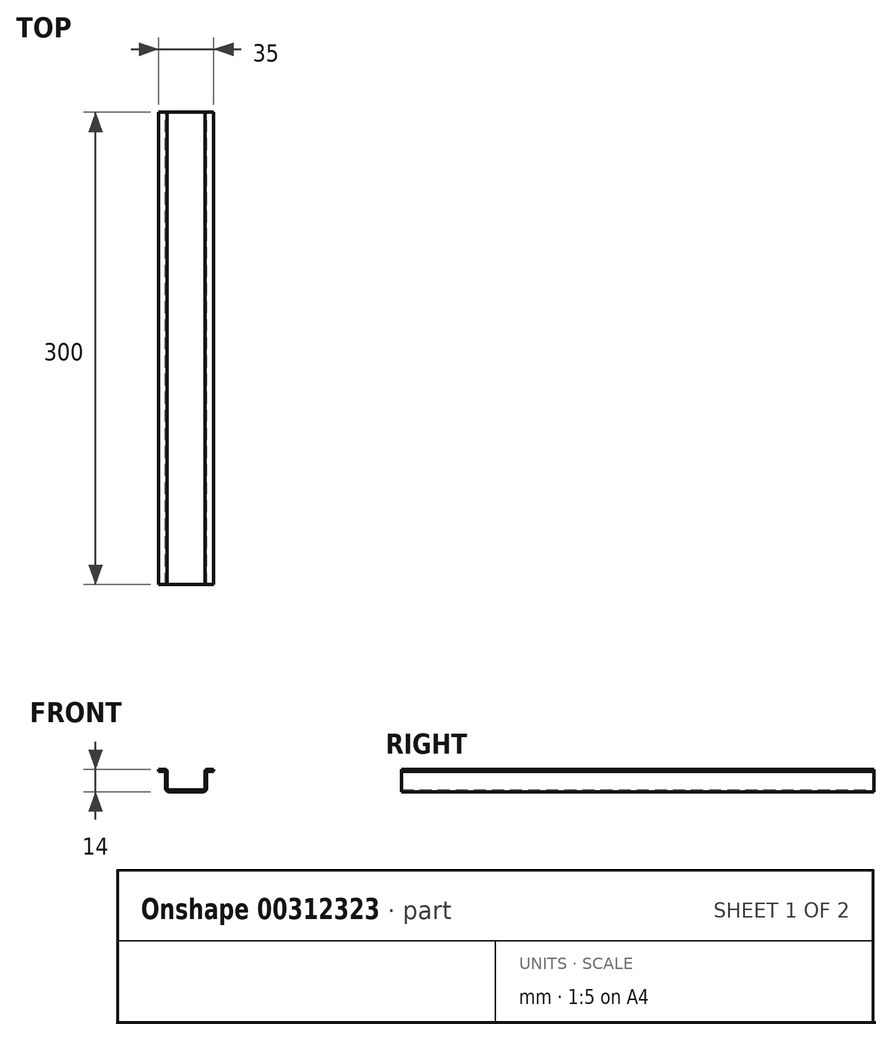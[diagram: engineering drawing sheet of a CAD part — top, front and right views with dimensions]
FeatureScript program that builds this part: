
annotation { "Feature Type Name" : "Feature", "Feature Type Description" : "" }
export const myFeature = defineFeature(function(context is Context, id is Id, definition is map)
    precondition{}
    {
        {
            var Q0;
            Q0=qCreatedBy(makeId("Front.planeOp"),FACE);
            var sketch = newSketch(context, id + "F0", { "sketchPlane" : qUnion([Q0])});
            skLineSegment(sketch, "E0", {"start": v(0, 0) * mm, "end": v(4.5, 0) * mm});
            skLineSegment(sketch, "E1", {"start": v(5.5, -1) * mm, "end": v(5.5, -12) * mm});
            skLineSegment(sketch, "E2", {"start": v(6.5, -13) * mm, "end": v(28.5, -13) * mm});
            skLineSegment(sketch, "E3", {"start": v(29.5, -12) * mm, "end": v(29.5, -1) * mm});
            skLineSegment(sketch, "E4", {"start": v(30.5, 0) * mm, "end": v(35, 0) * mm});
            skPoint(sketch, "E5.visualSharp", {"position": v(5.5, 0) * mm});
            skArc(sketch, "E5.filletArc", {"start": v(5.5, -1) * mm, "mid": v(5.2, -0.3) * mm, "end": v(4.5, 0) * mm});
            skPoint(sketch, "E6.visualSharp", {"position": v(5.5, -13) * mm});
            skArc(sketch, "E6.filletArc", {"start": v(5.5, -12) * mm, "mid": v(5.8, -12.7) * mm, "end": v(6.5, -13) * mm});
            skPoint(sketch, "E7.visualSharp", {"position": v(29.5, -13) * mm});
            skArc(sketch, "E7.filletArc", {"start": v(28.5, -13) * mm, "mid": v(29.2, -12.7) * mm, "end": v(29.5, -12) * mm});
            skPoint(sketch, "E8.visualSharp", {"position": v(29.5, 0) * mm});
            skArc(sketch, "E8.filletArc", {"start": v(30.5, 0) * mm, "mid": v(29.8, -0.3) * mm, "end": v(29.5, -1) * mm});
            skLineSegment(sketch, "E9.0", {"start": v(0, -1) * mm, "end": v(4.5, -1) * mm});
            skLineSegment(sketch, "E10.0", {"start": v(4.5, -1) * mm, "end": v(4.5, -12) * mm});
            skArc(sketch, "E11.0", {"start": v(4.5, -12) * mm, "mid": v(5.09, -13.41) * mm, "end": v(6.5, -14) * mm});
            skLineSegment(sketch, "E12.0", {"start": v(6.5, -14) * mm, "end": v(28.5, -14) * mm});
            skArc(sketch, "E13.0", {"start": v(28.5, -14) * mm, "mid": v(29.91, -13.41) * mm, "end": v(30.5, -12) * mm});
            skLineSegment(sketch, "E14.0", {"start": v(30.5, -12) * mm, "end": v(30.5, -1) * mm});
            skLineSegment(sketch, "E15.0", {"start": v(30.5, -1) * mm, "end": v(35, -1) * mm});
            skLineSegment(sketch, "E16", {"start": v(0, 0) * mm, "end": v(0, -1) * mm});
            skLineSegment(sketch, "E17", {"start": v(35, 0) * mm, "end": v(35, -1) * mm});
            skSolve(sketch);
        }
        {
            var Q0;
            Q0=qSketchRegion(id+"F0",true);
            extrude(context, id + "F1", {"entities" : qUnion([Q0]), "depth" : 300 * mm});
        }
    });
